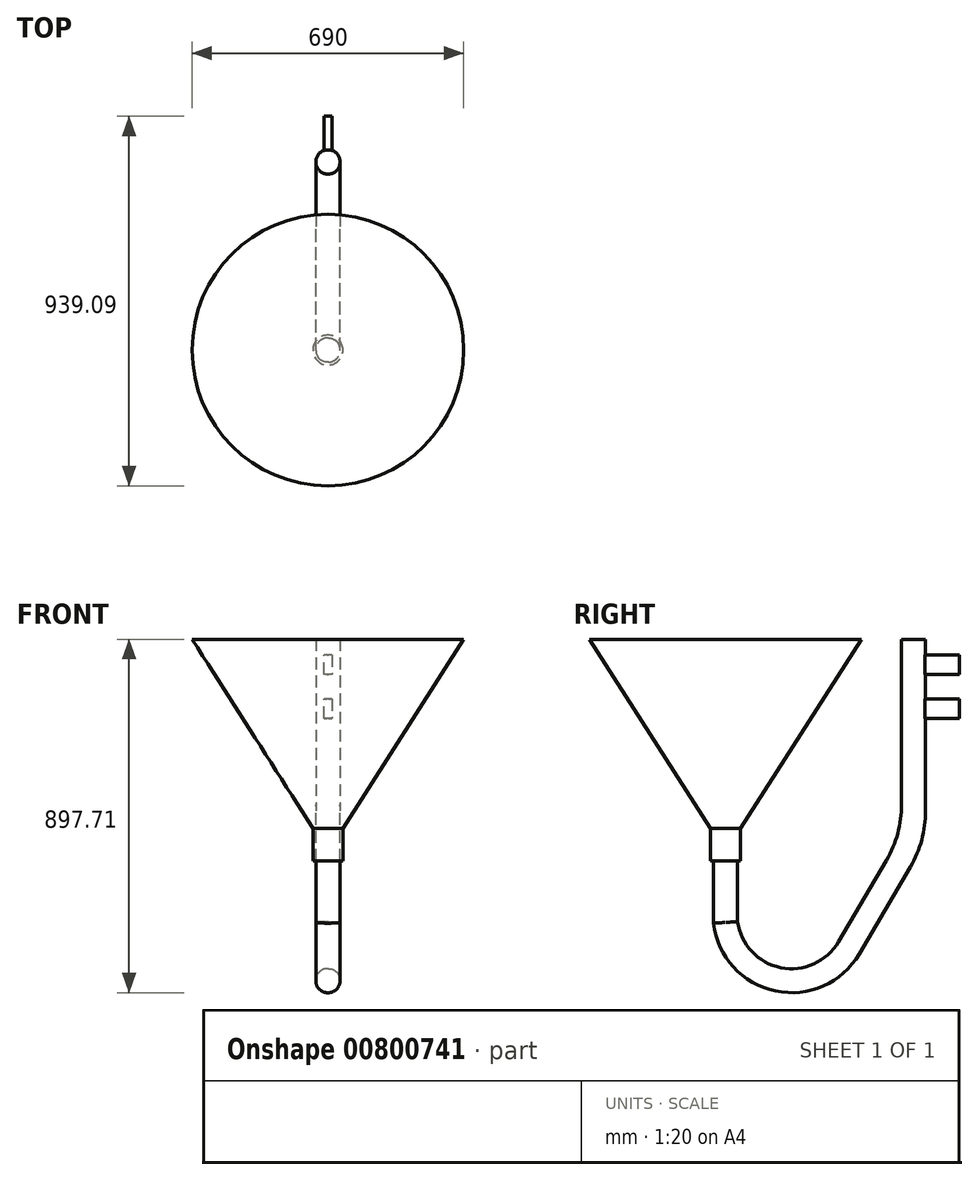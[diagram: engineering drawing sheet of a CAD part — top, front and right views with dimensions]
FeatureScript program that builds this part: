
annotation { "Feature Type Name" : "Feature", "Feature Type Description" : "" }
export const myFeature = defineFeature(function(context is Context, id is Id, definition is map)
    precondition{}
    {
        {
            var Q0;
            Q0=qCreatedBy(makeId("Right.planeOp"),FACE);
            var sketch = newSketch(context, id + "F0", { "sketchPlane" : qUnion([Q0])});
            skLineSegment(sketch, "E0", {"start": v(0, 0) * mm, "end": v(0, 563) * mm});
            skLineSegment(sketch, "E1", {"start": v(0, 563) * mm, "end": v(345, 563) * mm});
            skLineSegment(sketch, "E2", {"start": v(0, 0) * mm, "end": v(38, 0) * mm});
            skLineSegment(sketch, "E3", {"start": v(38, 0) * mm, "end": v(38, 83) * mm});
            skLineSegment(sketch, "E4", {"start": v(38, 83) * mm, "end": v(345, 563) * mm});
            skSolve(sketch);
        }
        {
            var Q0;
            Q0=makeQuery(id+"F0.imprint","IMPRINT",FACE,{"disambiguationData":[TD([[makeQuery(id+"F0.imprint","IMPRINT",EDGE,{"derivedFrom":sQuery(id+"F0.wireOp",EDGE,"E0")}),-1.0]])]});
            var Q1;
            Q1=sQuery(id+"F0.wireOp",EDGE,"E0");
            revolve(context, id + "F1", {"surfaceOperationType" : NewSurfaceOperationType.NEW, "entities" : qUnion([Q0]), "axis" : qUnion([Q1]), "revolveType" : RevolveType.FULL});
        }
        {
            var Q0;
            Q0=qCreatedBy(makeId("Right.planeOp"),FACE);
            var sketch = newSketch(context, id + "F2", { "sketchPlane" : qUnion([Q0])});
            skLineSegment(sketch, "E5", {"start": v(345, 563) * mm, "end": v(38, 83) * mm});
            skLineSegment(sketch, "E6", {"start": v(-38, 83) * mm, "end": v(-345, 563) * mm});
            skLineSegment(sketch, "E7", {"start": v(-38, 0) * mm, "end": v(-38, 83) * mm});
            skLineSegment(sketch, "E8", {"start": v(38, 83) * mm, "end": v(38, 0) * mm});
            skLineSegment(sketch, "E9", {"start": v(477.9, 563) * mm, "end": v(477.9, 59.34) * mm});
            skArc(sketch, "E10", {"start": v(0, -156.26) * mm, "mid": v(133.77, -300.77) * mm, "end": v(313.66, -220.68) * mm});
            skLineSegment(sketch, "E11", {"start": v(477.9, 59.34) * mm, "end": v(313.66, -220.68) * mm});
            skLineSegment(sketch, "E12", {"start": v(0, 0) * mm, "end": v(0, -156.26) * mm});
            skLineSegment(sketch, "E13.0", {"start": v(508.38, 563) * mm, "end": v(508.38, 51.06) * mm});
            skLineSegment(sketch, "E13.1", {"start": v(508.38, 51.06) * mm, "end": v(339.95, -236.1) * mm});
            skArc(sketch, "E13.2", {"start": v(-30.48, -158.1) * mm, "mid": v(126.66, -330.43) * mm, "end": v(339.95, -236.1) * mm});
            skLineSegment(sketch, "E13.3", {"start": v(-30.48, 0) * mm, "end": v(-30.48, -158.1) * mm});
            skLineSegment(sketch, "E14", {"start": v(-30.48, 0) * mm, "end": v(0, 0) * mm});
            skLineSegment(sketch, "E15", {"start": v(477.9, 563) * mm, "end": v(508.38, 563) * mm});
            skLineSegment(sketch, "E16.0", {"start": v(447.42, 563) * mm, "end": v(447.42, 67.61) * mm});
            skLineSegment(sketch, "E16.1", {"start": v(447.42, 67.61) * mm, "end": v(287.37, -205.25) * mm});
            skArc(sketch, "E16.2", {"start": v(30.48, -154.25) * mm, "mid": v(140.8, -271.1) * mm, "end": v(287.37, -205.25) * mm});
            skLineSegment(sketch, "E16.3", {"start": v(30.48, 0) * mm, "end": v(30.48, -154.25) * mm});
            skLineSegment(sketch, "E17", {"start": v(0, 0) * mm, "end": v(30.48, 0) * mm});
            skLineSegment(sketch, "E18", {"start": v(477.9, 563) * mm, "end": v(447.42, 563) * mm});
            skSolve(sketch);
        }
        {
            var Q0;
            Q0=makeQuery(id+"F2.imprint","IMPRINT",FACE,{"disambiguationData":[TD([[makeQuery(id+"F2.imprint","IMPRINT",EDGE,{"derivedFrom":sQuery(id+"F2.wireOp",EDGE,"E9")}),-1.0]])]});
            var Q1;
            Q1=makeQuery(id+"F2.imprint","IMPRINT",FACE,{"disambiguationData":[TD([[makeQuery(id+"F2.imprint","IMPRINT",EDGE,{"derivedFrom":sQuery(id+"F2.wireOp",EDGE,"E9")}),1.0]])]});
            extrude(context, id + "F3", {"entities" : qUnion([Q0, Q1]), "operationType" : NewBodyOperationType.ADD, "endBound" : BoundingType.SYMMETRIC, "depth" : 60.96 * mm, "offsetDistance" : 25.4 * mm});
        }
        {
            var Q0;
            Q0=makeQuery(id+"F3.opExtrude","SWEPT_EDGE",EDGE,{"disambiguationData":[OSD([sQuery(id+"F2.wireOp",EDGE,"E13.0"),sQuery(id+"F2.wireOp",EDGE,"E13.1")])]});
            var Q1;
            Q1=makeQuery(id+"F3.opExtrude","SWEPT_EDGE",EDGE,{"disambiguationData":[OSD([sQuery(id+"F2.wireOp",EDGE,"E16.0"),sQuery(id+"F2.wireOp",EDGE,"E16.1")])]});
            fillet(context, id + "F4", {"entities" : qUnion([Q0, Q1]), "radius" : 280.4 * mm, "tangentPropagation" : true, "allowEdgeOverflow" : false});
        }
        {
            var Q0;
            Q0=makeQuery(id+"F3.opExtrude","CAP_EDGE",EDGE,{"disambiguationData":[OSD([sQuery(id+"F2.wireOp",EDGE,"E16.3")])],"isStart":false});
            var Q1;
            Q1=makeQuery(id+"F3.opExtrude","CAP_EDGE",EDGE,{"disambiguationData":[OSD([sQuery(id+"F2.wireOp",EDGE,"E13.3")])],"isStart":false});
            var Q2;
            Q2=makeQuery(id+"F3.opExtrude","CAP_EDGE",EDGE,{"disambiguationData":[OSD([sQuery(id+"F2.wireOp",EDGE,"E13.2")])],"isStart":false});
            var Q3;
            Q3=makeQuery(id+"F3.opExtrude","CAP_EDGE",EDGE,{"disambiguationData":[OSD([sQuery(id+"F2.wireOp",EDGE,"E16.2")])],"isStart":false});
            var Q4;
            Q4=makeQuery(id+"F3.opExtrude","CAP_EDGE",EDGE,{"disambiguationData":[OSD([sQuery(id+"F2.wireOp",EDGE,"E16.1")])],"isStart":false});
            var Q5;
            Q5=makeQuery(id+"F3.opExtrude","CAP_EDGE",EDGE,{"disambiguationData":[OSD([sQuery(id+"F2.wireOp",EDGE,"E13.1")])],"isStart":false});
            var Q6;
            {var subQ0=sQuery(id+"F2.wireOp",EDGE,"E13.1");var subQ1=sQuery(id+"F2.wireOp",EDGE,"E13.0");Q6=makeQuery(id+"F4.opFillet","BLEND_EDGE",EDGE,{"blendedFrom":[makeQuery(id+"F3.opExtrude","SWEPT_EDGE",EDGE,{"disambiguationData":[OSD([subQ1,subQ0])]}),makeQuery(id+"F3.opExtrude","CAP_FACE",FACE,{"disambiguationData":[OSD([subQ1,subQ0,sQuery(id+"F2.wireOp",EDGE,"E13.2"),sQuery(id+"F2.wireOp",EDGE,"E13.3"),sQuery(id+"F2.wireOp",EDGE,"E14"),sQuery(id+"F2.wireOp",EDGE,"E15"),sQuery(id+"F2.wireOp",EDGE,"E16.0"),sQuery(id+"F2.wireOp",EDGE,"E16.1"),sQuery(id+"F2.wireOp",EDGE,"E16.2"),sQuery(id+"F2.wireOp",EDGE,"E16.3"),sQuery(id+"F2.wireOp",EDGE,"E17"),sQuery(id+"F2.wireOp",EDGE,"E18")])],"isStart":false})],"blendedInto":[makeQuery(id+"F3.opExtrude","CAP_FACE",FACE,{"disambiguationData":[OSD([subQ1,subQ0,sQuery(id+"F2.wireOp",EDGE,"E13.2"),sQuery(id+"F2.wireOp",EDGE,"E13.3"),sQuery(id+"F2.wireOp",EDGE,"E14"),sQuery(id+"F2.wireOp",EDGE,"E15"),sQuery(id+"F2.wireOp",EDGE,"E16.0"),sQuery(id+"F2.wireOp",EDGE,"E16.1"),sQuery(id+"F2.wireOp",EDGE,"E16.2"),sQuery(id+"F2.wireOp",EDGE,"E16.3"),sQuery(id+"F2.wireOp",EDGE,"E17"),sQuery(id+"F2.wireOp",EDGE,"E18")])],"isStart":false})]});}
            var Q7;
            {var subQ0=sQuery(id+"F2.wireOp",EDGE,"E16.1");var subQ1=sQuery(id+"F2.wireOp",EDGE,"E16.0");Q7=makeQuery(id+"F4.opFillet","BLEND_EDGE",EDGE,{"blendedFrom":[makeQuery(id+"F3.opExtrude","SWEPT_EDGE",EDGE,{"disambiguationData":[OSD([subQ1,subQ0])]}),makeQuery(id+"F3.opExtrude","CAP_FACE",FACE,{"disambiguationData":[OSD([sQuery(id+"F2.wireOp",EDGE,"E13.0"),sQuery(id+"F2.wireOp",EDGE,"E13.1"),sQuery(id+"F2.wireOp",EDGE,"E13.2"),sQuery(id+"F2.wireOp",EDGE,"E13.3"),sQuery(id+"F2.wireOp",EDGE,"E14"),sQuery(id+"F2.wireOp",EDGE,"E15"),subQ1,subQ0,sQuery(id+"F2.wireOp",EDGE,"E16.2"),sQuery(id+"F2.wireOp",EDGE,"E16.3"),sQuery(id+"F2.wireOp",EDGE,"E17"),sQuery(id+"F2.wireOp",EDGE,"E18")])],"isStart":false})],"blendedInto":[makeQuery(id+"F3.opExtrude","CAP_FACE",FACE,{"disambiguationData":[OSD([sQuery(id+"F2.wireOp",EDGE,"E13.0"),sQuery(id+"F2.wireOp",EDGE,"E13.1"),sQuery(id+"F2.wireOp",EDGE,"E13.2"),sQuery(id+"F2.wireOp",EDGE,"E13.3"),sQuery(id+"F2.wireOp",EDGE,"E14"),sQuery(id+"F2.wireOp",EDGE,"E15"),subQ1,subQ0,sQuery(id+"F2.wireOp",EDGE,"E16.2"),sQuery(id+"F2.wireOp",EDGE,"E16.3"),sQuery(id+"F2.wireOp",EDGE,"E17"),sQuery(id+"F2.wireOp",EDGE,"E18")])],"isStart":false})]});}
            var Q8;
            Q8=makeQuery(id+"F3.opExtrude","CAP_EDGE",EDGE,{"disambiguationData":[OSD([sQuery(id+"F2.wireOp",EDGE,"E16.0")])],"isStart":false});
            var Q9;
            Q9=makeQuery(id+"F3.opExtrude","CAP_EDGE",EDGE,{"disambiguationData":[OSD([sQuery(id+"F2.wireOp",EDGE,"E13.0")])],"isStart":false});
            var Q10;
            Q10=makeQuery(id+"F3.opExtrude","CAP_EDGE",EDGE,{"disambiguationData":[OSD([sQuery(id+"F2.wireOp",EDGE,"E16.0")])],"isStart":true});
            var Q11;
            Q11=makeQuery(id+"F3.opExtrude","CAP_EDGE",EDGE,{"disambiguationData":[OSD([sQuery(id+"F2.wireOp",EDGE,"E13.0")])],"isStart":true});
            var Q12;
            {var subQ0=sQuery(id+"F2.wireOp",EDGE,"E13.1");var subQ1=sQuery(id+"F2.wireOp",EDGE,"E13.0");Q12=makeQuery(id+"F4.opFillet","BLEND_EDGE",EDGE,{"blendedFrom":[makeQuery(id+"F3.opExtrude","SWEPT_EDGE",EDGE,{"disambiguationData":[OSD([subQ1,subQ0])]}),makeQuery(id+"F3.opExtrude","CAP_FACE",FACE,{"disambiguationData":[OSD([subQ1,subQ0,sQuery(id+"F2.wireOp",EDGE,"E13.2"),sQuery(id+"F2.wireOp",EDGE,"E13.3"),sQuery(id+"F2.wireOp",EDGE,"E14"),sQuery(id+"F2.wireOp",EDGE,"E15"),sQuery(id+"F2.wireOp",EDGE,"E16.0"),sQuery(id+"F2.wireOp",EDGE,"E16.1"),sQuery(id+"F2.wireOp",EDGE,"E16.2"),sQuery(id+"F2.wireOp",EDGE,"E16.3"),sQuery(id+"F2.wireOp",EDGE,"E17"),sQuery(id+"F2.wireOp",EDGE,"E18")])],"isStart":true})],"blendedInto":[makeQuery(id+"F3.opExtrude","CAP_FACE",FACE,{"disambiguationData":[OSD([subQ1,subQ0,sQuery(id+"F2.wireOp",EDGE,"E13.2"),sQuery(id+"F2.wireOp",EDGE,"E13.3"),sQuery(id+"F2.wireOp",EDGE,"E14"),sQuery(id+"F2.wireOp",EDGE,"E15"),sQuery(id+"F2.wireOp",EDGE,"E16.0"),sQuery(id+"F2.wireOp",EDGE,"E16.1"),sQuery(id+"F2.wireOp",EDGE,"E16.2"),sQuery(id+"F2.wireOp",EDGE,"E16.3"),sQuery(id+"F2.wireOp",EDGE,"E17"),sQuery(id+"F2.wireOp",EDGE,"E18")])],"isStart":true})]});}
            var Q13;
            {var subQ0=sQuery(id+"F2.wireOp",EDGE,"E16.1");var subQ1=sQuery(id+"F2.wireOp",EDGE,"E16.0");Q13=makeQuery(id+"F4.opFillet","BLEND_EDGE",EDGE,{"blendedFrom":[makeQuery(id+"F3.opExtrude","SWEPT_EDGE",EDGE,{"disambiguationData":[OSD([subQ1,subQ0])]}),makeQuery(id+"F3.opExtrude","CAP_FACE",FACE,{"disambiguationData":[OSD([sQuery(id+"F2.wireOp",EDGE,"E13.0"),sQuery(id+"F2.wireOp",EDGE,"E13.1"),sQuery(id+"F2.wireOp",EDGE,"E13.2"),sQuery(id+"F2.wireOp",EDGE,"E13.3"),sQuery(id+"F2.wireOp",EDGE,"E14"),sQuery(id+"F2.wireOp",EDGE,"E15"),subQ1,subQ0,sQuery(id+"F2.wireOp",EDGE,"E16.2"),sQuery(id+"F2.wireOp",EDGE,"E16.3"),sQuery(id+"F2.wireOp",EDGE,"E17"),sQuery(id+"F2.wireOp",EDGE,"E18")])],"isStart":true})],"blendedInto":[makeQuery(id+"F3.opExtrude","CAP_FACE",FACE,{"disambiguationData":[OSD([sQuery(id+"F2.wireOp",EDGE,"E13.0"),sQuery(id+"F2.wireOp",EDGE,"E13.1"),sQuery(id+"F2.wireOp",EDGE,"E13.2"),sQuery(id+"F2.wireOp",EDGE,"E13.3"),sQuery(id+"F2.wireOp",EDGE,"E14"),sQuery(id+"F2.wireOp",EDGE,"E15"),subQ1,subQ0,sQuery(id+"F2.wireOp",EDGE,"E16.2"),sQuery(id+"F2.wireOp",EDGE,"E16.3"),sQuery(id+"F2.wireOp",EDGE,"E17"),sQuery(id+"F2.wireOp",EDGE,"E18")])],"isStart":true})]});}
            var Q14;
            Q14=makeQuery(id+"F3.opExtrude","CAP_EDGE",EDGE,{"disambiguationData":[OSD([sQuery(id+"F2.wireOp",EDGE,"E13.1")])],"isStart":true});
            var Q15;
            Q15=makeQuery(id+"F3.opExtrude","CAP_EDGE",EDGE,{"disambiguationData":[OSD([sQuery(id+"F2.wireOp",EDGE,"E13.2")])],"isStart":true});
            var Q16;
            Q16=makeQuery(id+"F3.opExtrude","CAP_EDGE",EDGE,{"disambiguationData":[OSD([sQuery(id+"F2.wireOp",EDGE,"E16.2")])],"isStart":true});
            var Q17;
            Q17=makeQuery(id+"F3.opExtrude","CAP_EDGE",EDGE,{"disambiguationData":[OSD([sQuery(id+"F2.wireOp",EDGE,"E13.3")])],"isStart":true});
            var Q18;
            Q18=makeQuery(id+"F3.opExtrude","CAP_EDGE",EDGE,{"disambiguationData":[OSD([sQuery(id+"F2.wireOp",EDGE,"E16.3")])],"isStart":true});
            var Q19;
            Q19=makeQuery(id+"F3.opExtrude","CAP_EDGE",EDGE,{"disambiguationData":[OSD([sQuery(id+"F2.wireOp",EDGE,"E16.1")])],"isStart":true});
            fillet(context, id + "F5", {"entities" : qUnion([Q0, Q1, Q2, Q3, Q4, Q5, Q6, Q7, Q8, Q9, Q10, Q11, Q12, Q13, Q14, Q15, Q16, Q17, Q18, Q19]), "radius" : 28.82 * mm, "tangentPropagation" : true, "allowEdgeOverflow" : false});
        }
        {
            var Q0;
            Q0=qCreatedBy(makeId("Right.planeOp"),FACE);
            var sketch = newSketch(context, id + "F6", { "sketchPlane" : qUnion([Q0])});
            skLineSegment(sketch, "E19.bottom", {"start": v(495.23, 523.01) * mm, "end": v(594.09, 523.01) * mm});
            skLineSegment(sketch, "E19.top", {"start": v(495.23, 474.2) * mm, "end": v(594.09, 474.2) * mm});
            skLineSegment(sketch, "E19.left", {"start": v(495.23, 523.01) * mm, "end": v(495.23, 474.2) * mm});
            skLineSegment(sketch, "E19.right", {"start": v(594.09, 523.01) * mm, "end": v(594.09, 474.2) * mm});
            skLineSegment(sketch, "E20.bottom", {"start": v(594.09, 411.22) * mm, "end": v(495.23, 411.22) * mm});
            skLineSegment(sketch, "E20.top", {"start": v(594.09, 362.4) * mm, "end": v(495.23, 362.4) * mm});
            skLineSegment(sketch, "E20.left", {"start": v(594.09, 411.22) * mm, "end": v(594.09, 362.4) * mm});
            skLineSegment(sketch, "E20.right", {"start": v(495.23, 411.22) * mm, "end": v(495.23, 362.4) * mm});
            skSolve(sketch);
        }
        {
            var Q0;
            Q0=makeQuery(id+"F6.imprint","IMPRINT",FACE,{"disambiguationData":[TD([[makeQuery(id+"F6.imprint","IMPRINT",EDGE,{"derivedFrom":sQuery(id+"F6.wireOp",EDGE,"E19.bottom")}),-1.0]])]});
            var Q1;
            Q1=makeQuery(id+"F6.imprint","IMPRINT",FACE,{"disambiguationData":[TD([[makeQuery(id+"F6.imprint","IMPRINT",EDGE,{"derivedFrom":sQuery(id+"F6.wireOp",EDGE,"E20.bottom")}),1.0]])]});
            extrude(context, id + "F7", {"entities" : qUnion([Q0, Q1]), "operationType" : NewBodyOperationType.ADD, "endBound" : BoundingType.SYMMETRIC, "depth" : 20 * mm, "offsetDistance" : 25.4 * mm});
        }
    });
